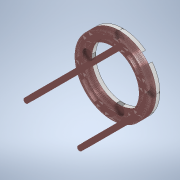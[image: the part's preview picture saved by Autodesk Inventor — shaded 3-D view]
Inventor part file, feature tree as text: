
AUTODESK INVENTOR PART (.ipt)
format: ipt  version: 2022.4 (Build 264492010, 492A)  size: 396,288 bytes
history: native  units: mm
features: sketch x4, extrude x3, other x2, plane x1
ambient origin geometry x8: Origin, YZ Plane, XZ Plane, XY Plane, X Axis, Y Axis, Z Axis, Center Point
bodies: Solid1 (feature_tree)
feature tree (10):
  other  "holder"
  sketch  "Sketch1"  dims[d0=11.0mm d1=40.0mm d3=360.0deg]
  extrude  "Extrusion1"  Depth=40.0mm TaperAngle=360.0deg
  extrude  "Extrusion2"  Depth=3.5mm TaperAngle=0.0deg
  sketch  "Sketch3"  dims[d5=4.0mm d6=0.0mm d7=3.5mm d8=0.0mm]
  sketch  "Sketch4"  dims[d9=135.0deg d10=90.0deg]
  plane  "Work Plane1"
  extrude  "Extrusion3"  TaperAngle=90.0deg  [1 undecoded]
  sketch  "Sketch5"  dims[d11=10.0mm d12=0.0mm]
  other  "MeshFeature1"
note: 1 required parameter value undecoded (feature->parameter linkage not recoverable at this tier; creation-order binding heuristic only, values carry confidence <= 0.55)
